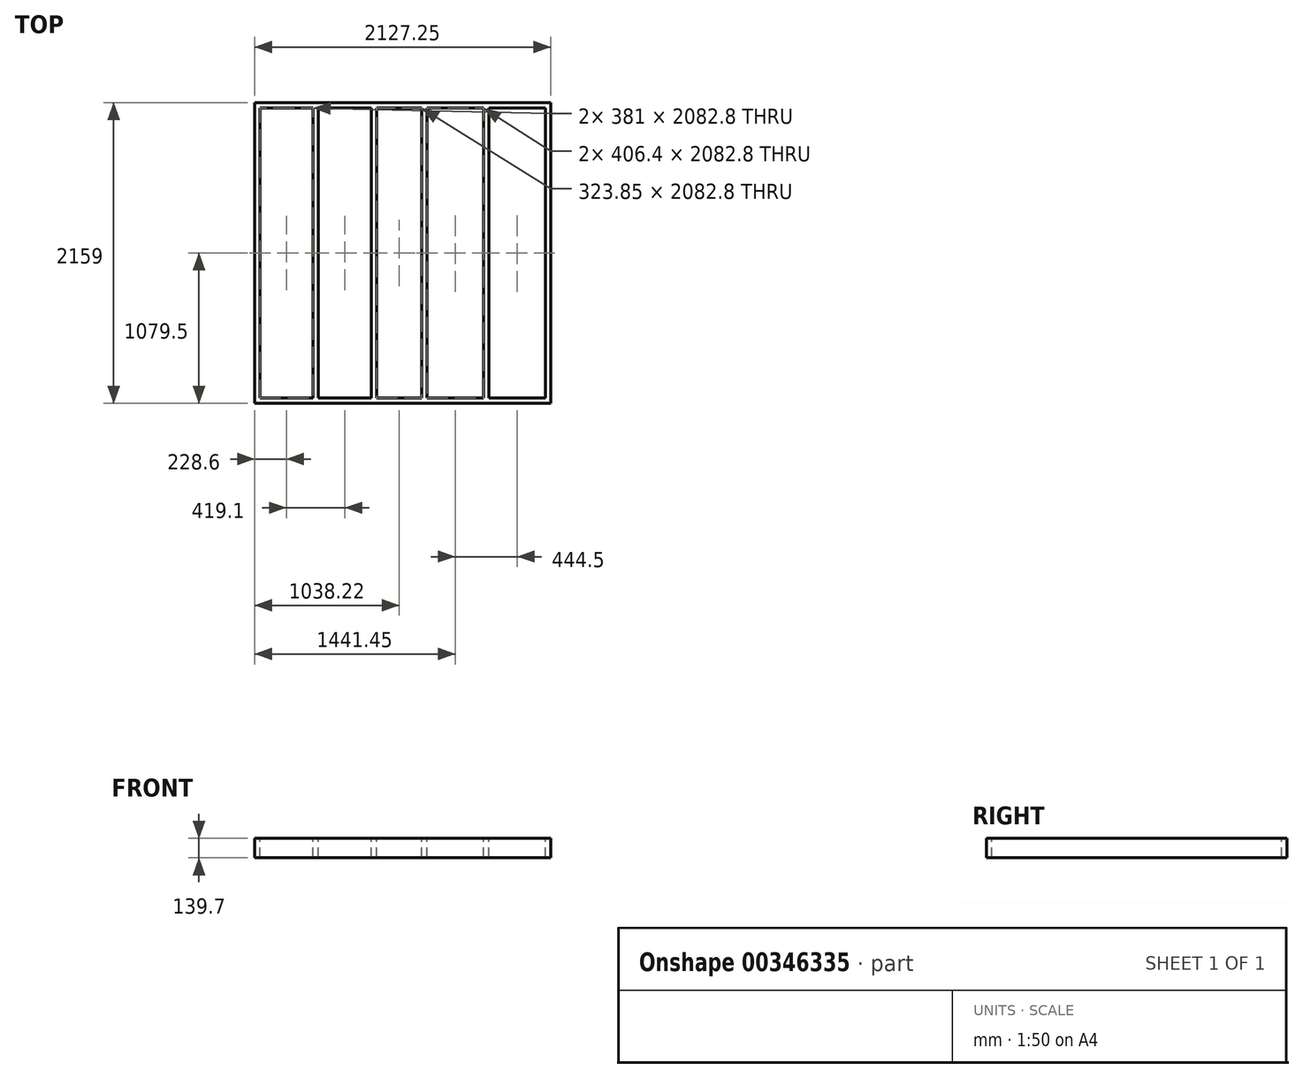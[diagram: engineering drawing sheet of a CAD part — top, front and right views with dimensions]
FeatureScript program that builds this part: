
annotation { "Feature Type Name" : "Feature", "Feature Type Description" : "" }
export const myFeature = defineFeature(function(context is Context, id is Id, definition is map)
    precondition{}
    {
        {
            var Q0;
            Q0=qCreatedBy(makeId("Top.planeOp"),FACE);
            var sketch = newSketch(context, id + "F0", { "sketchPlane" : qUnion([Q0])});
            skLineSegment(sketch, "E0.bottom", {"start": v(0, 0) * mm, "end": v(2127.25, 0) * mm});
            skLineSegment(sketch, "E0.top", {"start": v(0, -2159) * mm, "end": v(2127.25, -2159) * mm});
            skLineSegment(sketch, "E0.left", {"start": v(0, 0) * mm, "end": v(0, -2159) * mm});
            skLineSegment(sketch, "E0.right", {"start": v(2127.25, 0) * mm, "end": v(2127.25, -2159) * mm});
            skLineSegment(sketch, "E1", {"start": v(38.1, -2120.9) * mm, "end": v(419.1, -2120.9) * mm});
            skLineSegment(sketch, "E2", {"start": v(38.1, -38.1) * mm, "end": v(419.1, -38.1) * mm});
            skLineSegment(sketch, "E3", {"start": v(38.1, -38.1) * mm, "end": v(38.1, -2120.9) * mm});
            skLineSegment(sketch, "E4", {"start": v(419.1, -38.1) * mm, "end": v(419.1, -2120.9) * mm});
            skLineSegment(sketch, "E5", {"start": v(457.2, -38.1) * mm, "end": v(457.2, -2120.9) * mm});
            skLineSegment(sketch, "E6", {"start": v(838.2, -38.1) * mm, "end": v(838.2, -2120.9) * mm});
            skLineSegment(sketch, "E7", {"start": v(876.3, -38.1) * mm, "end": v(876.3, -2120.9) * mm});
            skLineSegment(sketch, "E8.MirrorCS", {"start": v(1200.15, -38.1) * mm, "end": v(1200.15, -2120.9) * mm});
            skLineSegment(sketch, "E9.MirrorCS", {"start": v(1238.25, -38.1) * mm, "end": v(1238.25, -2120.9) * mm});
            skLineSegment(sketch, "E10.MirrorCS", {"start": v(1644.65, -38.1) * mm, "end": v(1644.65, -2120.9) * mm});
            skLineSegment(sketch, "E11.MirrorCS", {"start": v(1682.75, -38.1) * mm, "end": v(1682.75, -2120.9) * mm});
            skLineSegment(sketch, "E12", {"start": v(2089.15, -38.1) * mm, "end": v(2089.15, -2120.9) * mm});
            skLineSegment(sketch, "E13.trimOffspring", {"start": v(457.2, -38.1) * mm, "end": v(838.2, -38.1) * mm});
            skLineSegment(sketch, "E14.trimOffspring", {"start": v(876.3, -38.1) * mm, "end": v(1200.15, -38.1) * mm});
            skLineSegment(sketch, "E15.trimOffspring", {"start": v(457.2, -2120.9) * mm, "end": v(838.2, -2120.9) * mm});
            skLineSegment(sketch, "E16.trimOffspring", {"start": v(876.3, -2120.9) * mm, "end": v(1200.15, -2120.9) * mm});
            skLineSegment(sketch, "E17.trimOffspring", {"start": v(1238.25, -2120.9) * mm, "end": v(1644.65, -2120.9) * mm});
            skLineSegment(sketch, "E18.trimOffspring", {"start": v(1682.75, -2120.9) * mm, "end": v(2089.15, -2120.9) * mm});
            skLineSegment(sketch, "E19.trimOffspring", {"start": v(1238.25, -38.1) * mm, "end": v(1644.65, -38.1) * mm});
            skLineSegment(sketch, "E20.trimOffspring", {"start": v(1682.75, -38.1) * mm, "end": v(2089.15, -38.1) * mm});
            skSolve(sketch);
        }
        {
            var Q0;
            Q0 = qSketchRegion(id + "F0", true);
            extrude(context, id + "F1", {"entities" : qUnion([Q0]), "oppositeDirection" : true, "depth" : 139.7 * mm});
        }
    });
